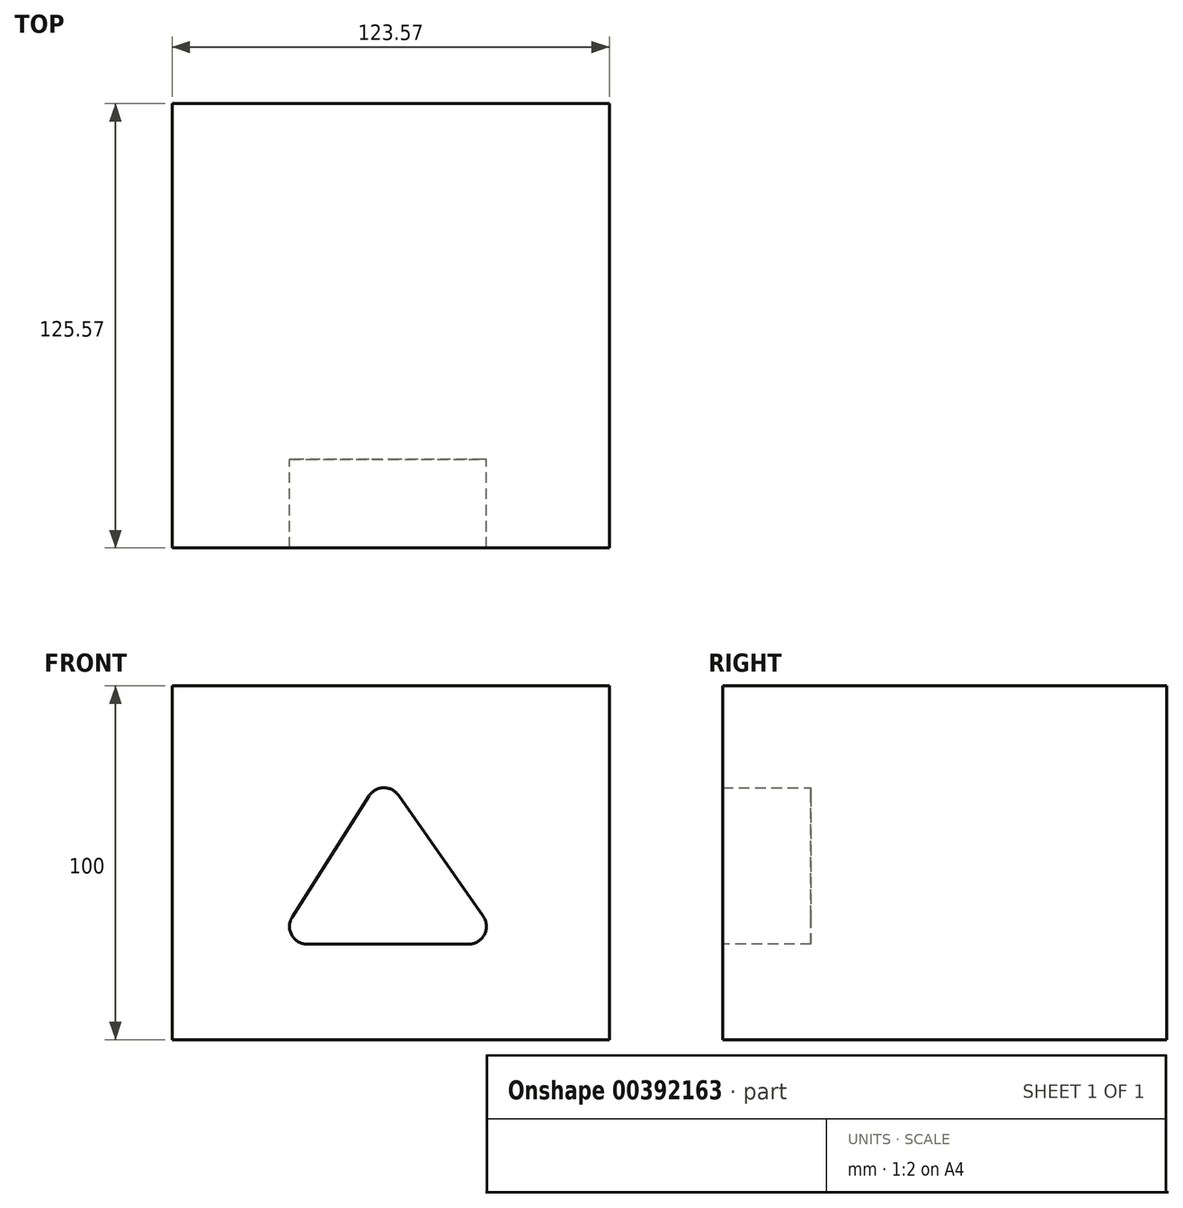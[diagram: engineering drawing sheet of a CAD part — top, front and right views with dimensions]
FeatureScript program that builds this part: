
annotation { "Feature Type Name" : "Feature", "Feature Type Description" : "" }
export const myFeature = defineFeature(function(context is Context, id is Id, definition is map)
    precondition{}
    {
        {
            var Q0;
            Q0=qCreatedBy(makeId("Top.planeOp"),FACE);
            var sketch = newSketch(context, id + "F0", { "sketchPlane" : qUnion([Q0])});
            skLineSegment(sketch, "E0.bottom", {"start": v(-59.7, 66.05) * mm, "end": v(63.87, 66.05) * mm});
            skLineSegment(sketch, "E0.top", {"start": v(-59.7, -59.52) * mm, "end": v(63.87, -59.52) * mm});
            skLineSegment(sketch, "E0.left", {"start": v(-59.7, 66.05) * mm, "end": v(-59.7, -59.52) * mm});
            skLineSegment(sketch, "E0.right", {"start": v(63.87, 66.05) * mm, "end": v(63.87, -59.52) * mm});
            skSolve(sketch);
        }
        {
            var Q0;
            Q0=makeQuery(id+"F0.imprint","IMPRINT",FACE,{"disambiguationData":[TD([[makeQuery(id+"F0.imprint","IMPRINT",EDGE,{"derivedFrom":sQuery(id+"F0.wireOp",EDGE,"E0.bottom")}),-1.0]])]});
            extrude(context, id + "F1", {"entities" : qUnion([Q0]), "depth" : 100 * mm});
        }
        {
            var Q0;
            Q0=makeQuery(id+"F1.opExtrude","SWEPT_FACE",FACE,{"disambiguationData":[OSD([sQuery(id+"F0.wireOp",EDGE,"E0.top")])]});
            var sketch = newSketch(context, id + "F2", { "sketchPlane" : qUnion([Q0])});
            skLineSegment(sketch, "E1", {"start": v(-30.61, 27) * mm, "end": v(33.72, 27) * mm});
            skLineSegment(sketch, "E2", {"start": v(33.72, 27) * mm, "end": v(0, 75.2) * mm});
            skLineSegment(sketch, "E3", {"start": v(0, 75.2) * mm, "end": v(-30.61, 27) * mm});
            skSolve(sketch);
        }
        {
            var Q0;
            Q0=makeQuery(id+"F2.imprint","IMPRINT",FACE,{"disambiguationData":[TD([[makeQuery(id+"F2.imprint","IMPRINT",EDGE,{"derivedFrom":sQuery(id+"F2.wireOp",EDGE,"E1")}),1.0]])]});
            extrude(context, id + "F3", {"entities" : qUnion([Q0]), "operationType" : NewBodyOperationType.REMOVE, "oppositeDirection" : true, "depth" : 25 * mm});
        }
        {
            var Q0;
            Q0=makeQuery(id+"F3.boolean.opBoolean","COPY",EDGE,{"derivedFrom":makeQuery(id+"F3.opExtrude","SWEPT_EDGE",EDGE,{"disambiguationData":[OSD([sQuery(id+"F2.wireOp",EDGE,"E2"),sQuery(id+"F2.wireOp",EDGE,"E3")])]})});
            var Q1;
            Q1=makeQuery(id+"F3.boolean.opBoolean","COPY",EDGE,{"derivedFrom":makeQuery(id+"F3.opExtrude","SWEPT_EDGE",EDGE,{"disambiguationData":[OSD([sQuery(id+"F2.wireOp",EDGE,"E1"),sQuery(id+"F2.wireOp",EDGE,"E3")])]})});
            var Q2;
            Q2=makeQuery(id+"F3.boolean.opBoolean","COPY",EDGE,{"derivedFrom":makeQuery(id+"F3.opExtrude","SWEPT_EDGE",EDGE,{"disambiguationData":[OSD([sQuery(id+"F2.wireOp",EDGE,"E1"),sQuery(id+"F2.wireOp",EDGE,"E2")])]})});
            fillet(context, id + "F4", {"entities" : qUnion([Q0, Q1, Q2]), "radius" : 5 * mm, "tangentPropagation" : true, "allowEdgeOverflow" : false});
        }
    });
